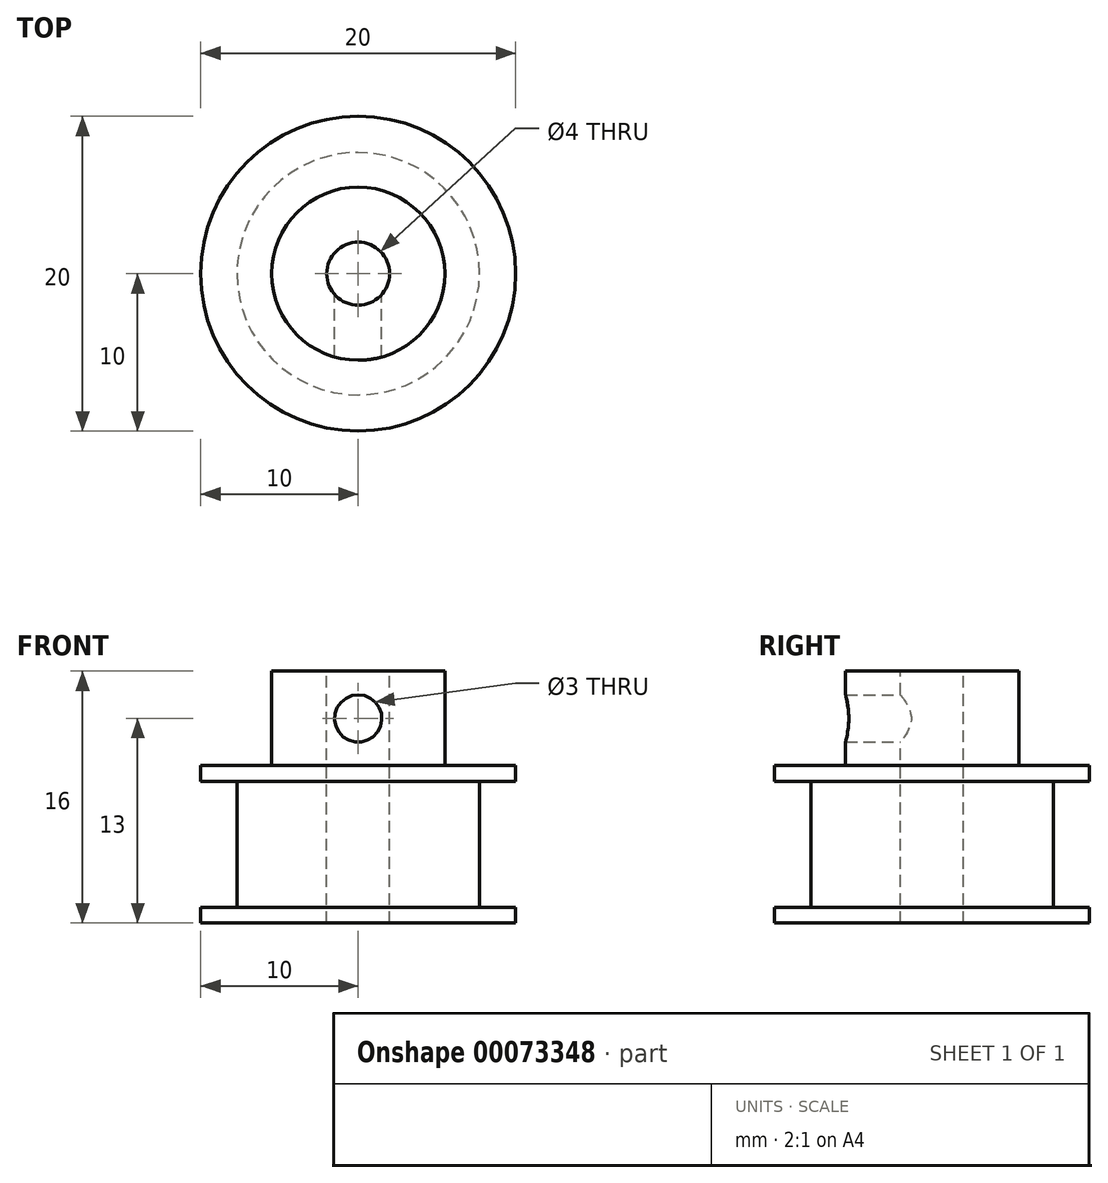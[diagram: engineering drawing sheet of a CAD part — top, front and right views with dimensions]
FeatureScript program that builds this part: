
annotation { "Feature Type Name" : "Feature", "Feature Type Description" : "" }
export const myFeature = defineFeature(function(context is Context, id is Id, definition is map)
    precondition{}
    {
        {
            var Q0;
            Q0=qCreatedBy(makeId("Top.planeOp"),FACE);
            var sketch = newSketch(context, id + "F0", { "sketchPlane" : qUnion([Q0])});
            skCircle(sketch, "E0", {"center": v(0, 0) * mm, "radius": 7.7 * mm});
            skSolve(sketch);
        }
        {
            var Q0;
            Q0=makeQuery(id+"F0.imprint","IMPRINT",FACE,{"disambiguationData":[TD([[makeQuery(id+"F0.imprint","IMPRINT",EDGE,{"derivedFrom":sQuery(id+"F0.wireOp",EDGE,"E0")}),1.0]])]});
            extrude(context, id + "F1", {"entities" : qUnion([Q0]), "depth" : 8 * mm, "offsetDistance" : 25 * mm, "symmetric" : true});
        }
        {
            var Q0;
            Q0=makeQuery(id+"F1.opExtrude","CAP_FACE",FACE,{"disambiguationData":[OSD([sQuery(id+"F0.wireOp",EDGE,"E0")])],"isStart":false});
            var sketch = newSketch(context, id + "F2", { "sketchPlane" : qUnion([Q0])});
            skCircle(sketch, "E1", {"center": v(0, 0) * mm, "radius": 10 * mm});
            skSolve(sketch);
        }
        {
            var Q0;
            Q0=makeQuery(id+"F2.imprint","IMPRINT",FACE,{"disambiguationData":[TD([[makeQuery(id+"F2.imprint","IMPRINT",EDGE,{"derivedFrom":sQuery(id+"F2.wireOp",EDGE,"E1")}),1.0]])]});
            var Q1;
            Q1=makeQuery(id+"F2.imprint","IMPRINT",FACE,{"disambiguationData":[TD([[makeQuery(id+"F2.imprint","IMPRINT",EDGE,{"derivedFrom":makeQuery(id+"F1.opExtrude","CAP_EDGE",EDGE,{"disambiguationData":[OSD([sQuery(id+"F0.wireOp",EDGE,"E0")])],"isStart":false})}),1.0]])]});
            extrude(context, id + "F3", {"entities" : qUnion([Q0, Q1]), "operationType" : NewBodyOperationType.ADD, "depth" : 1 * mm, "offsetDistance" : 25 * mm});
        }
        {
            var Q0;
            Q0=makeQuery(id+"F1.opExtrude","CAP_FACE",FACE,{"disambiguationData":[OSD([sQuery(id+"F0.wireOp",EDGE,"E0")])],"isStart":true});
            var sketch = newSketch(context, id + "F4", { "sketchPlane" : qUnion([Q0])});
            skCircle(sketch, "E2", {"center": v(0, 0) * mm, "radius": 10 * mm});
            skSolve(sketch);
        }
        {
            var Q0;
            Q0=makeQuery(id+"F4.imprint","IMPRINT",FACE,{"disambiguationData":[TD([[makeQuery(id+"F4.imprint","IMPRINT",EDGE,{"derivedFrom":makeQuery(id+"F1.opExtrude","CAP_EDGE",EDGE,{"disambiguationData":[OSD([sQuery(id+"F0.wireOp",EDGE,"E0")])],"isStart":true})}),-1.0]])]});
            var Q1;
            Q1=makeQuery(id+"F4.imprint","IMPRINT",FACE,{"disambiguationData":[TD([[makeQuery(id+"F4.imprint","IMPRINT",EDGE,{"derivedFrom":sQuery(id+"F4.wireOp",EDGE,"E2")}),1.0]])]});
            extrude(context, id + "F5", {"entities" : qUnion([Q0, Q1]), "operationType" : NewBodyOperationType.ADD, "depth" : 1 * mm, "offsetDistance" : 25 * mm});
        }
        {
            var Q0;
            Q0=makeQuery(id+"F3.opExtrude","CAP_FACE",FACE,{"disambiguationData":[OSD([sQuery(id+"F2.wireOp",EDGE,"E1")])],"isStart":false});
            var sketch = newSketch(context, id + "F6", { "sketchPlane" : qUnion([Q0])});
            skCircle(sketch, "E3", {"center": v(0, 0) * mm, "radius": 5.5 * mm});
            skSolve(sketch);
        }
        {
            var Q0;
            Q0=makeQuery(id+"F6.imprint","IMPRINT",FACE,{"disambiguationData":[TD([[makeQuery(id+"F6.imprint","IMPRINT",EDGE,{"derivedFrom":sQuery(id+"F6.wireOp",EDGE,"E3")}),1.0]])]});
            extrude(context, id + "F7", {"entities" : qUnion([Q0]), "operationType" : NewBodyOperationType.ADD, "depth" : (16 - 10) * mm, "offsetDistance" : 25 * mm});
        }
        {
            var Q0;
            Q0=makeQuery(id+"F7.opExtrude","CAP_FACE",FACE,{"disambiguationData":[OSD([sQuery(id+"F6.wireOp",EDGE,"E3")])],"isStart":false});
            var sketch = newSketch(context, id + "F8", { "sketchPlane" : qUnion([Q0])});
            skPoint(sketch, "E4", {"position": v(0, 0) * mm});
            skSolve(sketch);
        }
        {
            var Q0;
            Q0=sQuery(id+"F8.wireOp",VERTEX,"E4");
            var Q1;
            Q1=makeQuery(id+"F1.opExtrude","SWEPT_BODY",BODY,{"disambiguationData":[OSD([sQuery(id+"F0.wireOp",EDGE,"E0")])]});
            hole(context, id + "F9", {"style" : HoleStyle.SIMPLE, "endStyle" : HoleEndStyle.THROUGH, "holeDiameter" : 4 * mm, "majorDiameter" : 5 * mm, "tappedDepth" : 12 * mm, "tapClearance" : 3, "locations" : qUnion([Q0]), "scope" : qUnion([Q1])});
        }
        {
            var Q0;
            Q0=qCreatedBy(makeId("Front.planeOp"),FACE);
            var sketch = newSketch(context, id + "F10", { "sketchPlane" : qUnion([Q0])});
            skCircle(sketch, "E5", {"center": v(0, 8) * mm, "radius": 1.5 * mm});
            skSolve(sketch);
        }
        {
            var Q0;
            Q0=makeQuery(id+"F10.imprint","IMPRINT",FACE,{"disambiguationData":[TD([[makeQuery(id+"F10.imprint","IMPRINT",EDGE,{"derivedFrom":sQuery(id+"F10.wireOp",EDGE,"E5")}),1.0]])]});
            extrude(context, id + "F11", {"entities" : qUnion([Q0]), "operationType" : NewBodyOperationType.REMOVE, "depth" : 25 * mm, "offsetDistance" : 25 * mm});
        }
    });
